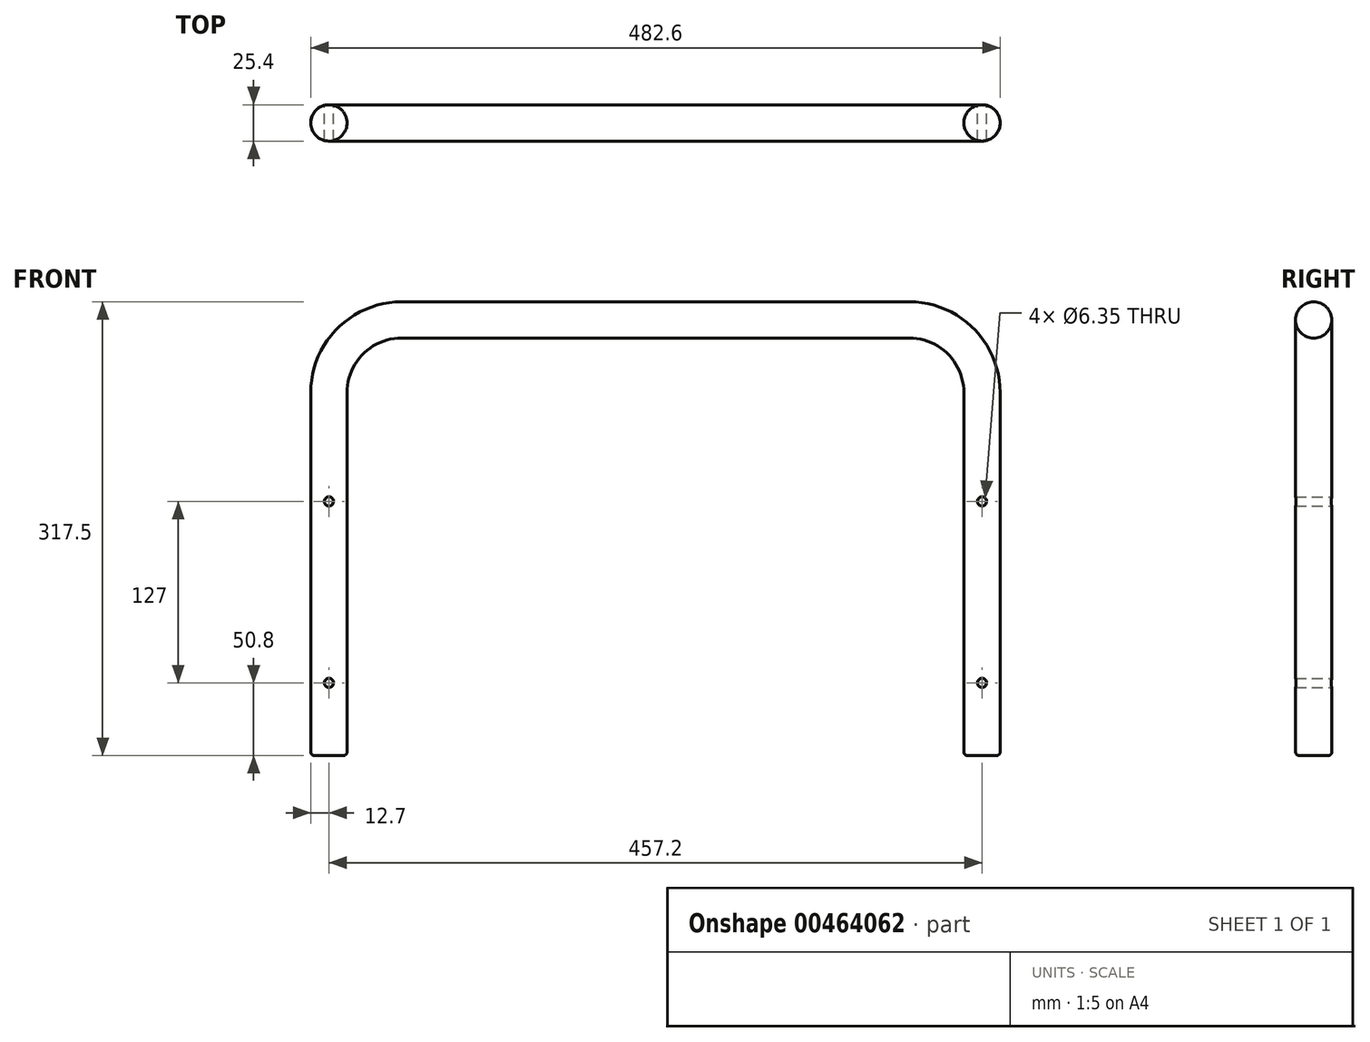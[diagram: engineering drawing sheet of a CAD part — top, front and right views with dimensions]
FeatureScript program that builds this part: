
annotation { "Feature Type Name" : "Feature", "Feature Type Description" : "" }
export const myFeature = defineFeature(function(context is Context, id is Id, definition is map)
    precondition{}
    {
        {
            var Q0;
            Q0=qCreatedBy(makeId("Top.planeOp"),FACE);
            var sketch = newSketch(context, id + "F0", { "sketchPlane" : qUnion([Q0])});
            skLineSegment(sketch, "E0", {"start": v(0, 0) * mm, "end": v(228.6, 0) * mm});
            skCircle(sketch, "E1", {"center": v(228.6, 0) * mm, "radius": 12.7 * mm});
            skLineSegment(sketch, "E2", {"start": v(0, 0) * mm, "end": v(-228.6, 0) * mm});
            skCircle(sketch, "E3", {"center": v(-228.6, 0) * mm, "radius": 12.7 * mm});
            skSolve(sketch);
        }
        {
            var Q0;
            Q0=qCreatedBy(makeId("Front.planeOp"),FACE);
            var sketch = newSketch(context, id + "F1", { "sketchPlane" : qUnion([Q0])});
            skLineSegment(sketch, "E4", {"start": v(0, 0) * mm, "end": v(-228.6, 0) * mm});
            skLineSegment(sketch, "E5", {"start": v(0, 0) * mm, "end": v(228.6, 0) * mm});
            skLineSegment(sketch, "E6", {"start": v(-228.6, 0) * mm, "end": v(-228.6, 254) * mm});
            skLineSegment(sketch, "E7", {"start": v(0, 304.8) * mm, "end": v(-177.8, 304.8) * mm});
            skArc(sketch, "E8", {"start": v(-177.8, 304.8) * mm, "mid": v(-213.72, 289.92) * mm, "end": v(-228.6, 254) * mm});
            skSolve(sketch);
        }
        {
            var Q0;
            Q0=makeQuery(id+"F0.imprint","IMPRINT",FACE,{"disambiguationData":[TD([[makeQuery(id+"F0.imprint","IMPRINT",EDGE,{"derivedFrom":sQuery(id+"F0.wireOp",EDGE,"E3")}),1.0]])]});
            var Q1;
            Q1=sQuery(id+"F1.wireOp",EDGE,"E8");
            var Q2;
            Q2=sQuery(id+"F1.wireOp",EDGE,"E7");
            var Q3;
            Q3=sQuery(id+"F1.wireOp",EDGE,"E6");
            sweep(context, id + "F2", {"profiles" : qUnion([Q0]), "path" : qUnion([Q1, Q2, Q3])});
        }
        {
            var Q0;
            Q0=makeQuery(id+"F2.opSweep","SWEPT_BODY",BODY,{"disambiguationData":[OSD([sQuery(id+"F0.wireOp",EDGE,"E1"),sQuery(id+"F1.wireOp",EDGE,"6a5d0813-440f-4a63-a660-ac133c4bdf6a0.MirrorCS")])]});
            var Q1;
            Q1=makeQuery(id+"F2.opSweep","SWEPT_BODY",BODY,{"disambiguationData":[OSD([sQuery(id+"F0.wireOp",EDGE,"E3"),sQuery(id+"F1.wireOp",EDGE,"E7")])]});
            var Q2;
            Q2=qCreatedBy(makeId("Right.planeOp"),FACE);
            mirror(context, id + "F3", {"operationType" : NewBodyOperationType.ADD, "entities" : qUnion([Q0, Q1]), "mirrorPlane" : qUnion([Q2])});
        }
        {
            var Q0;
            Q0=qCreatedBy(makeId("Front.planeOp"),FACE);
            var sketch = newSketch(context, id + "F4", { "sketchPlane" : qUnion([Q0])});
            skLineSegment(sketch, "E9", {"start": v(0, 0) * mm, "end": v(-228.6, 0) * mm});
            skLineSegment(sketch, "E10", {"start": v(-228.6, 0) * mm, "end": v(-228.6, 50.8) * mm});
            skLineSegment(sketch, "E11", {"start": v(-228.6, 50.8) * mm, "end": v(-228.6, 177.8) * mm});
            skCircle(sketch, "E12", {"center": v(-228.6, 177.8) * mm, "radius": 3.18 * mm});
            skCircle(sketch, "E13", {"center": v(-228.6, 50.8) * mm, "radius": 3.18 * mm});
            skLineSegment(sketch, "E14", {"start": v(0, 0) * mm, "end": v(0, 69.23) * mm});
            skCircle(sketch, "E15.MirrorC", {"center": v(228.6, 177.8) * mm, "radius": 3.18 * mm});
            skCircle(sketch, "E16.MirrorC", {"center": v(228.6, 50.8) * mm, "radius": 3.18 * mm});
            skSolve(sketch);
        }
        {
            var Q0;
            Q0 = qSketchRegion(id + "F4", true);
            extrude(context, id + "F5", {"entities" : qUnion([Q0]), "operationType" : NewBodyOperationType.REMOVE, "depth" : 25.4 * mm, "hasSecondDirection" : true, "secondDirectionOppositeDirection" : true, "secondDirectionDepth" : 25.4 * mm});
        }
        {
            var Q0;
            Q0=makeQuery(id+"F3.opPattern","COPY",EDGE,{"derivedFrom":makeQuery(id+"F2.opSweep","CAP_EDGE",EDGE,{"disambiguationData":[OSD([sQuery(id+"F0.wireOp",EDGE,"E1"),sQuery(id+"F1.wireOp",VERTEX,"6a5d0813-440f-4a63-a660-ac133c4bdf6a0.MirrorCS.start")])],"isStart":true}),"instanceName":"1"});
            var Q1;
            Q1=makeQuery(id+"F2.opSweep","CAP_EDGE",EDGE,{"disambiguationData":[OSD([sQuery(id+"F0.wireOp",EDGE,"E1"),sQuery(id+"F1.wireOp",VERTEX,"6a5d0813-440f-4a63-a660-ac133c4bdf6a0.MirrorCS.start")])],"isStart":true});
            var Q2;
            Q2=makeQuery(id+"F3.opPattern","COPY",EDGE,{"derivedFrom":makeQuery(id+"F2.opSweep","CAP_EDGE",EDGE,{"disambiguationData":[OSD([sQuery(id+"F0.wireOp",EDGE,"E3"),sQuery(id+"F1.wireOp",VERTEX,"E6.start")])],"isStart":true}),"instanceName":"1"});
            var Q3;
            Q3=makeQuery(id+"F2.opSweep","CAP_EDGE",EDGE,{"disambiguationData":[OSD([sQuery(id+"F0.wireOp",EDGE,"E3"),sQuery(id+"F1.wireOp",VERTEX,"E6.start")])],"isStart":true});
            fillet(context, id + "F6", {"entities" : qUnion([Q0, Q1, Q2, Q3]), "radius" : 2.54 * mm, "tangentPropagation" : true, "allowEdgeOverflow" : false});
        }
    });
